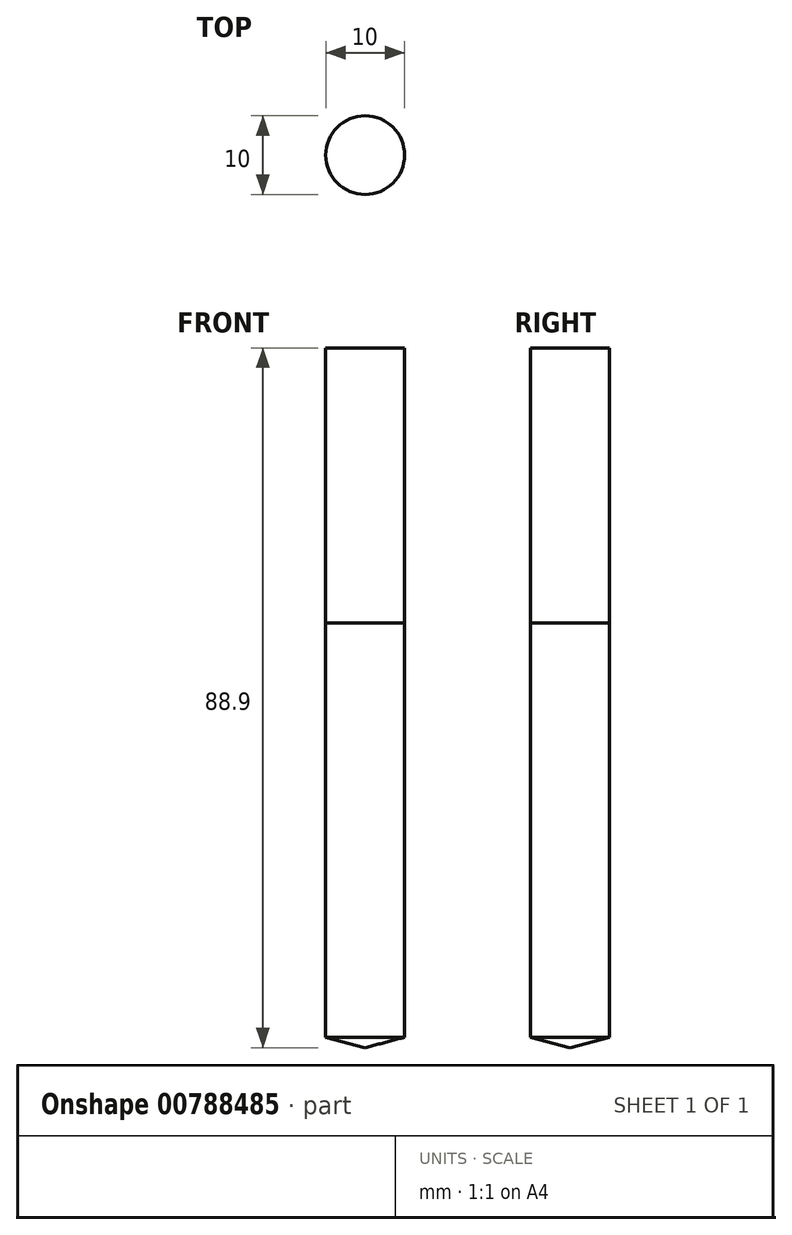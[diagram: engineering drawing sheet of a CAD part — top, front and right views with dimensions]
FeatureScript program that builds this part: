
annotation { "Feature Type Name" : "Feature", "Feature Type Description" : "" }
export const myFeature = defineFeature(function(context is Context, id is Id, definition is map)
    precondition{}
    {
        {
            var Q0;
            Q0=qCreatedBy(makeId("Front.planeOp"),FACE);
            var sketch = newSketch(context, id + "F0", { "sketchPlane" : qUnion([Q0])});
            skLineSegment(sketch, "E0", {"start": v(0, 0) * mm, "end": v(5, 0) * mm});
            skLineSegment(sketch, "E1", {"start": v(5, 0) * mm, "end": v(5, -87.56) * mm});
            skLineSegment(sketch, "E2", {"start": v(5, -87.56) * mm, "end": v(0, -88.9) * mm});
            skLineSegment(sketch, "E3", {"start": v(0, -88.9) * mm, "end": v(0, 0) * mm});
            skLineSegment(sketch, "E4", {"start": v(0, -34.92) * mm, "end": v(5, -34.92) * mm});
            skLineSegment(sketch, "E5", {"start": v(0, -88.9) * mm, "end": v(5, -88.9) * mm, "construction": true});
            skSolve(sketch);
        }
        {
            var Q0;
            {var subQ0=sQuery(id+"F0.wireOp",EDGE,"E0");Q0=makeQuery(id+"F0.imprint","IMPRINT",FACE,{"disambiguationData":[TD([[makeQuery(id+"F0.imprint","IMPRINT",EDGE,{"derivedFrom":subQ0}),-1.0]])]});}
            var Q1;
            Q1=sQuery(id+"F0.wireOp",EDGE,"E3");
            revolve(context, id + "F1", {"entities" : qUnion([Q0]), "axis" : qUnion([Q1]), "revolveType" : RevolveType.FULL});
        }
        {
            var Q0;
            {var subQ0=sQuery(id+"F0.wireOp",EDGE,"E2");Q0=makeQuery(id+"F0.imprint","IMPRINT",FACE,{"disambiguationData":[TD([[makeQuery(id+"F0.imprint","IMPRINT",EDGE,{"derivedFrom":subQ0}),-1.0]])]});}
            var Q1;
            Q1=sQuery(id+"F0.wireOp",EDGE,"E3");
            revolve(context, id + "F2", {"entities" : qUnion([Q0]), "axis" : qUnion([Q1]), "revolveType" : RevolveType.FULL});
        }
    });
